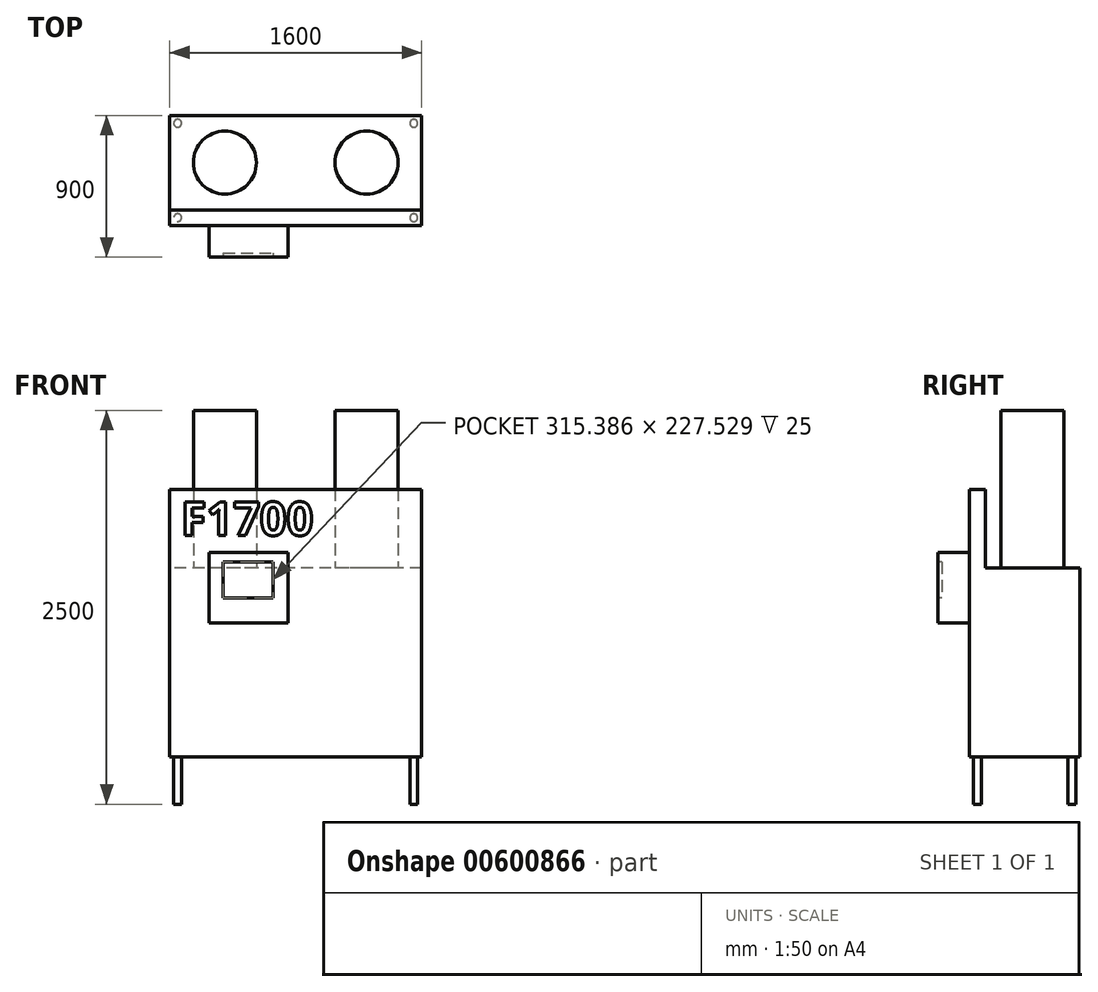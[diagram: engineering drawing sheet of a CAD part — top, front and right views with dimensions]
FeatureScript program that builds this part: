
annotation { "Feature Type Name" : "Feature", "Feature Type Description" : "" }
export const myFeature = defineFeature(function(context is Context, id is Id, definition is map)
    precondition{}
    {
        {
            var Q0;
            Q0=qCreatedBy(makeId("Front.planeOp"),FACE);
            var sketch = newSketch(context, id + "F0", { "sketchPlane" : qUnion([Q0])});
            skLineSegment(sketch, "E0.bottom", {"start": v(0, 0) * mm, "end": v(1600, 0) * mm});
            skLineSegment(sketch, "E0.top", {"start": v(0, 1700) * mm, "end": v(1600, 1700) * mm});
            skLineSegment(sketch, "E0.left", {"start": v(0, 0) * mm, "end": v(0, 1700) * mm});
            skLineSegment(sketch, "E0.right", {"start": v(1600, 0) * mm, "end": v(1600, 1700) * mm});
            skSolve(sketch);
        }
        {
            var Q0;
            Q0=makeQuery(id+"F0.imprint","IMPRINT",FACE,{"disambiguationData":[TD([[makeQuery(id+"F0.imprint","IMPRINT",EDGE,{"derivedFrom":sQuery(id+"F0.wireOp",EDGE,"E0.bottom")}),1.0]])]});
            extrude(context, id + "F1", {"entities" : qUnion([Q0]), "depth" : 100 * mm, "offsetDistance" : 25 * mm});
        }
        {
            var Q0;
            Q0=makeQuery(id+"F1.opExtrude","CAP_FACE",FACE,{"disambiguationData":[OSD([sQuery(id+"F0.wireOp",EDGE,"E0.bottom"),sQuery(id+"F0.wireOp",EDGE,"E0.top"),sQuery(id+"F0.wireOp",EDGE,"E0.left"),sQuery(id+"F0.wireOp",EDGE,"E0.right")])],"isStart":false});
            var sketch = newSketch(context, id + "F2", { "sketchPlane" : qUnion([Q0])});
            skLineSegment(sketch, "E1.bottom", {"start": v(250, 1300) * mm, "end": v(750, 1300) * mm});
            skLineSegment(sketch, "E1.top", {"start": v(250, 850) * mm, "end": v(750, 850) * mm});
            skLineSegment(sketch, "E1.left", {"start": v(250, 1300) * mm, "end": v(250, 850) * mm});
            skLineSegment(sketch, "E1.right", {"start": v(750, 1300) * mm, "end": v(750, 850) * mm});
            skSolve(sketch);
        }
        {
            var Q0;
            Q0=makeQuery(id+"F2.imprint","IMPRINT",FACE,{"disambiguationData":[TD([[makeQuery(id+"F2.imprint","IMPRINT",EDGE,{"derivedFrom":sQuery(id+"F2.wireOp",EDGE,"E1.bottom")}),-1.0]])]});
            extrude(context, id + "F3", {"entities" : qUnion([Q0]), "operationType" : NewBodyOperationType.ADD, "depth" : 200 * mm, "offsetDistance" : 25 * mm});
        }
        {
            var Q0;
            Q0=makeQuery(id+"F1.opExtrude","CAP_FACE",FACE,{"disambiguationData":[OSD([sQuery(id+"F0.wireOp",EDGE,"E0.bottom"),sQuery(id+"F0.wireOp",EDGE,"E0.top"),sQuery(id+"F0.wireOp",EDGE,"E0.left"),sQuery(id+"F0.wireOp",EDGE,"E0.right")])],"isStart":true});
            var sketch = newSketch(context, id + "F4", { "sketchPlane" : qUnion([Q0])});
            skLineSegment(sketch, "E2.bottom", {"start": v(-1600, 0) * mm, "end": v(0, 0) * mm});
            skLineSegment(sketch, "E2.top", {"start": v(-1600, 1200) * mm, "end": v(0, 1200) * mm});
            skLineSegment(sketch, "E2.left", {"start": v(-1600, 0) * mm, "end": v(-1600, 1200) * mm});
            skLineSegment(sketch, "E2.right", {"start": v(0, 0) * mm, "end": v(0, 1200) * mm});
            skSolve(sketch);
        }
        {
            var Q0;
            Q0=makeQuery(id+"F4.imprint","IMPRINT",FACE,{"disambiguationData":[TD([[makeQuery(id+"F4.imprint","IMPRINT",EDGE,{"derivedFrom":sQuery(id+"F4.wireOp",EDGE,"E2.bottom")}),-1.0]])]});
            extrude(context, id + "F5", {"entities" : qUnion([Q0]), "operationType" : NewBodyOperationType.ADD, "depth" : 600 * mm, "offsetDistance" : 25 * mm});
        }
        {
            var Q0;
            Q0=makeQuery(id+"F5.opExtrude","SWEPT_FACE",FACE,{"disambiguationData":[OSD([sQuery(id+"F4.wireOp",EDGE,"E2.top")])]});
            var sketch = newSketch(context, id + "F6", { "sketchPlane" : qUnion([Q0])});
            skCircle(sketch, "E3", {"center": v(350, 300) * mm, "radius": 200 * mm});
            skCircle(sketch, "E4", {"center": v(1250, 300) * mm, "radius": 200 * mm});
            skSolve(sketch);
        }
        {
            var Q0;
            Q0 = qSketchRegion(id + "F6", true);
            extrude(context, id + "F7", {"entities" : qUnion([Q0]), "operationType" : NewBodyOperationType.ADD, "depth" : 1000 * mm, "offsetDistance" : 25 * mm});
        }
        {
            var Q0;
            Q0=makeQuery(id+"F5.boolean.opBoolean","MERGE",FACE,{"derivedFrom":[makeQuery(id+"F1.opExtrude","SWEPT_FACE",FACE,{"disambiguationData":[OSD([sQuery(id+"F0.wireOp",EDGE,"E0.bottom")])]}),makeQuery(id+"F5.opExtrude","SWEPT_FACE",FACE,{"disambiguationData":[OSD([sQuery(id+"F4.wireOp",EDGE,"E2.bottom")])]})]});
            var sketch = newSketch(context, id + "F8", { "sketchPlane" : qUnion([Q0])});
            skCircle(sketch, "E5", {"center": v(50, 50) * mm, "radius": 25 * mm});
            skCircle(sketch, "E6", {"center": v(1550, 50) * mm, "radius": 25 * mm});
            skCircle(sketch, "E7", {"center": v(50, -550) * mm, "radius": 25 * mm});
            skCircle(sketch, "E8", {"center": v(1550, -550) * mm, "radius": 25 * mm});
            skSolve(sketch);
        }
        {
            var Q0;
            Q0 = qSketchRegion(id + "F8", true);
            extrude(context, id + "F9", {"entities" : qUnion([Q0]), "operationType" : NewBodyOperationType.ADD, "depth" : 300 * mm, "offsetDistance" : 25 * mm});
        }
        {
            var Q0;
            Q0=makeQuery(id+"F3.opExtrude","CAP_FACE",FACE,{"disambiguationData":[OSD([sQuery(id+"F2.wireOp",EDGE,"E1.bottom"),sQuery(id+"F2.wireOp",EDGE,"E1.top"),sQuery(id+"F2.wireOp",EDGE,"E1.left"),sQuery(id+"F2.wireOp",EDGE,"E1.right")])],"isStart":false});
            var sketch = newSketch(context, id + "F10", { "sketchPlane" : qUnion([Q0])});
            skLineSegment(sketch, "E9.bottom", {"start": v(339.31, 1238.29) * mm, "end": v(654.7, 1238.29) * mm});
            skLineSegment(sketch, "E9.top", {"start": v(339.31, 1010.76) * mm, "end": v(654.7, 1010.76) * mm});
            skLineSegment(sketch, "E9.left", {"start": v(339.31, 1238.29) * mm, "end": v(339.31, 1010.76) * mm});
            skLineSegment(sketch, "E9.right", {"start": v(654.7, 1238.29) * mm, "end": v(654.7, 1010.76) * mm});
            skSolve(sketch);
        }
        {
            var Q0;
            Q0=makeQuery(id+"F10.imprint","IMPRINT",FACE,{"disambiguationData":[TD([[makeQuery(id+"F10.imprint","IMPRINT",EDGE,{"derivedFrom":sQuery(id+"F10.wireOp",EDGE,"E9.bottom")}),-1.0]])]});
            extrude(context, id + "F11", {"entities" : qUnion([Q0]), "operationType" : NewBodyOperationType.REMOVE, "oppositeDirection" : true, "depth" : 25 * mm, "offsetDistance" : 25 * mm});
        }
        {
            var Q0;
            Q0=makeQuery(id+"F1.opExtrude","CAP_FACE",FACE,{"disambiguationData":[OSD([sQuery(id+"F0.wireOp",EDGE,"E0.bottom"),sQuery(id+"F0.wireOp",EDGE,"E0.top"),sQuery(id+"F0.wireOp",EDGE,"E0.left"),sQuery(id+"F0.wireOp",EDGE,"E0.right")])],"isStart":false});
            var sketch = newSketch(context, id + "F12", { "sketchPlane" : qUnion([Q0])});
            skText(sketch, "E10", { "text": "F1700", "fontName": "OpenSans-Bold.ttf"});
            const initialGuessF12  = {"E10": [0.0697, 1.40675, 1, 0, 0.2139]};
            skSetInitialGuess(sketch, initialGuessF12);
            skSolve(sketch);
        }
        {
            var Q0;
            Q0 = qSketchRegion(id + "F12", true);
            extrude(context, id + "F13", {"entities" : qUnion([Q0]), "operationType" : NewBodyOperationType.ADD, "depth" : 1 * mm, "offsetDistance" : 25 * mm});
        }
    });
